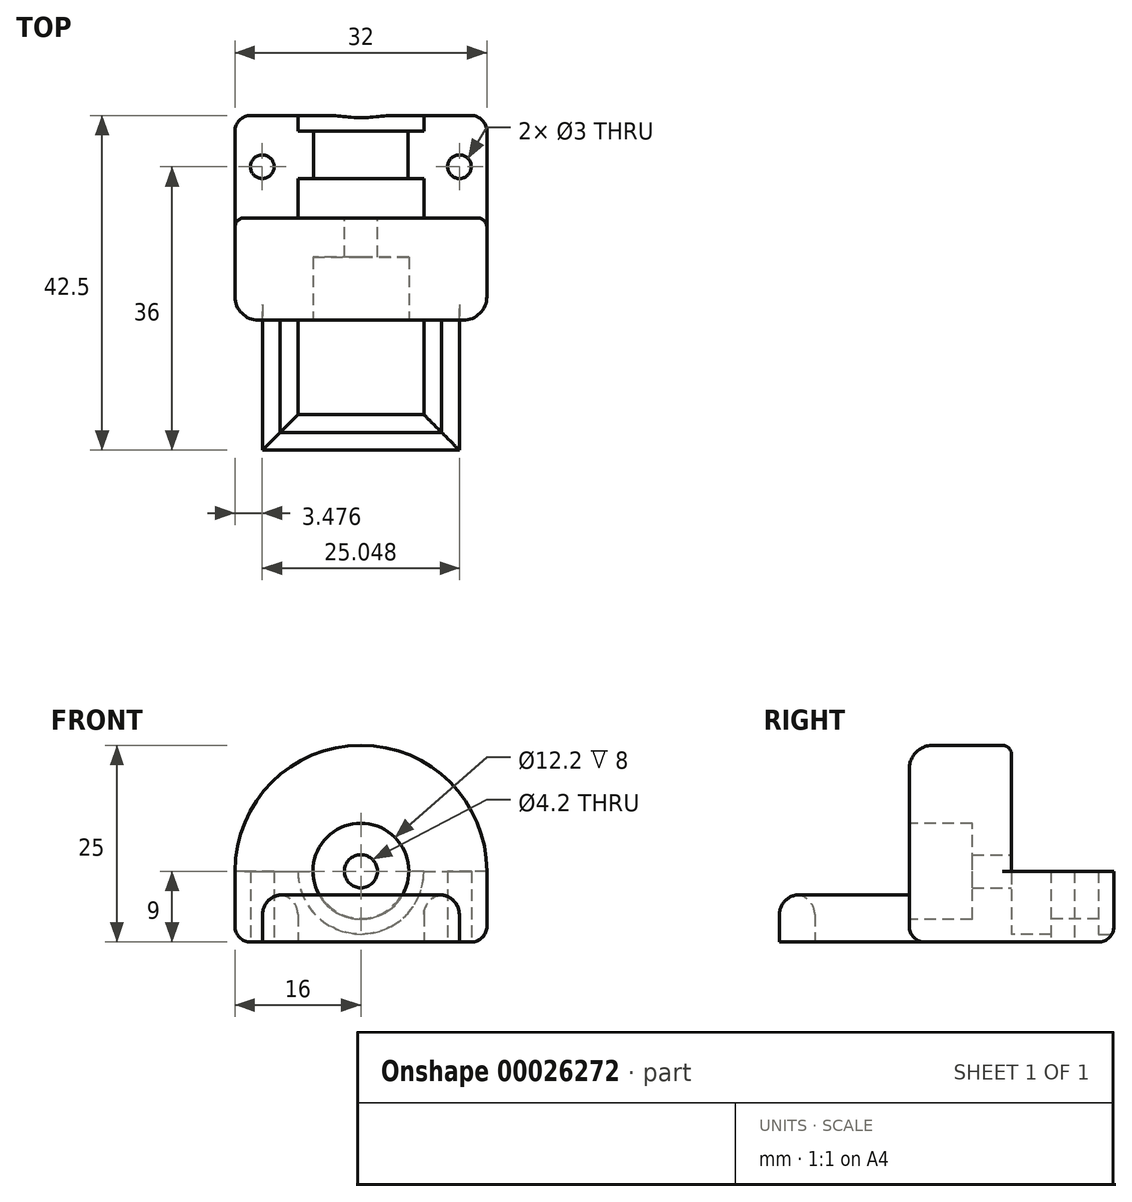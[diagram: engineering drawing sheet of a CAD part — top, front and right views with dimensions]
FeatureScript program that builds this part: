
annotation { "Feature Type Name" : "Feature", "Feature Type Description" : "" }
export const myFeature = defineFeature(function(context is Context, id is Id, definition is map)
    precondition{}
    {
        {
            var Q0;
            Q0=qCreatedBy(makeId("Top.planeOp"),FACE);
            var sketch = newSketch(context, id + "F0", { "sketchPlane" : qUnion([Q0])});
            skLineSegment(sketch, "E0.rect.bottom", {"start": v(-16, 6.5) * mm, "end": v(16, 6.5) * mm});
            skLineSegment(sketch, "E0.rect.top", {"start": v(-16, -6.5) * mm, "end": v(16, -6.5) * mm});
            skLineSegment(sketch, "E0.rect.left", {"start": v(-16, 6.5) * mm, "end": v(-16, -6.5) * mm});
            skLineSegment(sketch, "E0.rect.right", {"start": v(16, 6.5) * mm, "end": v(16, -6.5) * mm});
            skPoint(sketch, "E0.rect.middle", {"position": v(0, 0) * mm});
            skCircle(sketch, "E1", {"center": v(12.52, 0) * mm, "radius": 1.5 * mm});
            skCircle(sketch, "E2", {"center": v(-12.52, 0) * mm, "radius": 1.5 * mm});
            skSolve(sketch);
        }
        {
            var Q0;
            Q0=makeQuery(id+"F0.imprint","IMPRINT",FACE,{"disambiguationData":[TD([[makeQuery(id+"F0.imprint","IMPRINT",EDGE,{"derivedFrom":sQuery(id+"F0.wireOp",EDGE,"E0.rect.bottom")}),-1.0]])]});
            extrude(context, id + "F1", {"entities" : qUnion([Q0]), "depth" : 9 * mm});
        }
        {
            var Q0;
            Q0=makeQuery(id+"F1.opExtrude","SWEPT_FACE",FACE,{"disambiguationData":[OSD([sQuery(id+"F0.wireOp",EDGE,"E0.rect.top")])]});
            var sketch = newSketch(context, id + "F2", { "sketchPlane" : qUnion([Q0])});
            skCircle(sketch, "E3", {"center": v(0, 9) * mm, "radius": 8 * mm});
            skSolve(sketch);
        }
        {
            var Q0;
            Q0=qSketchRegion(id+"F2",true);
            var Q1;
            Q1=makeQuery(id+"F1.opExtrude","SWEPT_FACE",FACE,{"disambiguationData":[OSD([sQuery(id+"F0.wireOp",EDGE,"E0.rect.bottom")])]});
            extrude(context, id + "F3", {"entities" : qUnion([Q0, Q1]), "operationType" : NewBodyOperationType.REMOVE, "oppositeDirection" : true, "depth" : 5 * mm});
        }
        {
            var Q0;
            Q0=makeQuery(id+"F1.opExtrude","SWEPT_FACE",FACE,{"disambiguationData":[OSD([sQuery(id+"F0.wireOp",EDGE,"E0.rect.bottom")])]});
            var sketch = newSketch(context, id + "F4", { "sketchPlane" : qUnion([Q0])});
            skCircle(sketch, "E4", {"center": v(0, 9) * mm, "radius": 8 * mm});
            skSolve(sketch);
        }
        {
            var Q0;
            Q0=qSketchRegion(id+"F4",true);
            extrude(context, id + "F5", {"entities" : qUnion([Q0]), "operationType" : NewBodyOperationType.REMOVE, "oppositeDirection" : true, "depth" : 2 * mm});
        }
        {
            var Q0;
            Q0=makeQuery(id+"F5.boolean.opBoolean","COPY",FACE,{"derivedFrom":makeQuery(id+"F5.opExtrude","CAP_FACE",FACE,{"disambiguationData":[OSD([sQuery(id+"F4.wireOp",EDGE,"E4")])],"isStart":false})});
            var sketch = newSketch(context, id + "F6", { "sketchPlane" : qUnion([Q0])});
            skCircle(sketch, "E5", {"center": v(0, 9) * mm, "radius": 6 * mm});
            skSolve(sketch);
        }
        {
            var Q0;
            Q0=qSketchRegion(id+"F6",true);
            extrude(context, id + "F7", {"entities" : qUnion([Q0]), "operationType" : NewBodyOperationType.REMOVE, "oppositeDirection" : true, "depth" : 25 * mm});
        }
        {
            var Q0;
            Q0=makeQuery(id+"F1.opExtrude","CAP_EDGE",EDGE,{"disambiguationData":[OSD([sQuery(id+"F0.wireOp",EDGE,"E0.rect.bottom")])],"isStart":true});
            var Q1;
            Q1=makeQuery(id+"F7.boolean.opBoolean","COPY",EDGE,{"derivedFrom":makeQuery(id+"F7.opExtrude","CAP_EDGE",EDGE,{"disambiguationData":[OSD([sQuery(id+"F6.wireOp",EDGE,"E5")])],"isStart":true})});
            var Q2;
            Q2=makeQuery(id+"F1.opExtrude","SWEPT_EDGE",EDGE,{"disambiguationData":[OSD([sQuery(id+"F0.wireOp",EDGE,"E0.rect.bottom"),sQuery(id+"F0.wireOp",EDGE,"E0.rect.left")])]});
            var Q3;
            Q3=makeQuery(id+"F1.opExtrude","CAP_EDGE",EDGE,{"disambiguationData":[OSD([sQuery(id+"F0.wireOp",EDGE,"E0.rect.left")])],"isStart":true});
            var Q4;
            Q4=makeQuery(id+"F1.opExtrude","CAP_EDGE",EDGE,{"disambiguationData":[OSD([sQuery(id+"F0.wireOp",EDGE,"E0.rect.right")])],"isStart":true});
            var Q5;
            Q5=makeQuery(id+"F1.opExtrude","SWEPT_EDGE",EDGE,{"disambiguationData":[OSD([sQuery(id+"F0.wireOp",EDGE,"E0.rect.bottom"),sQuery(id+"F0.wireOp",EDGE,"E0.rect.right")])]});
            fillet(context, id + "F8", {"entities" : qUnion([Q0, Q1, Q2, Q3, Q4, Q5]), "radius" : 2 * mm, "tangentPropagation" : true, "allowEdgeOverflow" : false});
        }
        {
            var Q0;
            Q0=makeQuery(id+"F1.opExtrude","SWEPT_FACE",FACE,{"disambiguationData":[OSD([sQuery(id+"F0.wireOp",EDGE,"E0.rect.top")])]});
            var sketch = newSketch(context, id + "F9", { "sketchPlane" : qUnion([Q0])});
            skArc(sketch, "E6", {"start": v(16, 9) * mm, "mid": v(0, 25) * mm, "end": v(-16, 9) * mm});
            skLineSegment(sketch, "E7", {"start": v(0, 0) * mm, "end": v(13.23, 0) * mm});
            skLineSegment(sketch, "E8", {"start": v(-13.23, 0) * mm, "end": v(0, 0) * mm});
            skLineSegment(sketch, "E9", {"start": v(-16, 9) * mm, "end": v(-16, 0) * mm});
            skLineSegment(sketch, "E10", {"start": v(16, 9) * mm, "end": v(16, 0) * mm});
            skLineSegment(sketch, "E11", {"start": v(-16, 0) * mm, "end": v(16, 0) * mm});
            skSolve(sketch);
        }
        {
            var Q0;
            Q0=qSketchRegion(id+"F9",true);
            extrude(context, id + "F10", {"entities" : qUnion([Q0]), "operationType" : NewBodyOperationType.ADD, "depth" : 13 * mm});
        }
        {
            var Q0;
            Q0=qCreatedBy(makeId("Top.planeOp"),FACE);
            var sketch = newSketch(context, id + "F11", { "sketchPlane" : qUnion([Q0])});
            skLineSegment(sketch, "E12", {"start": v(-8, -19.5) * mm, "end": v(-12.5, -19.5) * mm});
            skLineSegment(sketch, "E13", {"start": v(-12.5, -19.5) * mm, "end": v(-8, -19.5) * mm});
            skLineSegment(sketch, "E14", {"start": v(12.5, -19.5) * mm, "end": v(12.5, -36) * mm});
            skLineSegment(sketch, "E15", {"start": v(12.5, -36) * mm, "end": v(-12.5, -36) * mm});
            skLineSegment(sketch, "E16", {"start": v(-12.5, -36) * mm, "end": v(-12.5, -19.5) * mm});
            skLineSegment(sketch, "E17", {"start": v(-8, -19.5) * mm, "end": v(-8, -31.5) * mm});
            skLineSegment(sketch, "E18", {"start": v(-8, -31.5) * mm, "end": v(8, -31.5) * mm});
            skLineSegment(sketch, "E19", {"start": v(8, -31.5) * mm, "end": v(8, -19.5) * mm});
            skLineSegment(sketch, "E20.trimOffspring", {"start": v(8, -19.5) * mm, "end": v(12.5, -19.5) * mm});
            skPoint(sketch, "E21.orphan", {"position": v(0, -19.5) * mm});
            skPoint(sketch, "E22", {"position": v(0, -31.5) * mm});
            skPoint(sketch, "E23", {"position": v(0, -36) * mm});
            skSolve(sketch);
        }
        {
            var Q0;
            Q0=qSketchRegion(id+"F11",true);
            extrude(context, id + "F12", {"entities" : qUnion([Q0]), "operationType" : NewBodyOperationType.ADD, "depth" : 6 * mm});
        }
        {
            var Q0;
            Q0=makeQuery(id+"F12.opExtrude","CAP_EDGE",EDGE,{"disambiguationData":[OSD([sQuery(id+"F11.wireOp",EDGE,"E17")])],"isStart":false});
            var Q1;
            Q1=makeQuery(id+"F12.opExtrude","CAP_EDGE",EDGE,{"disambiguationData":[OSD([sQuery(id+"F11.wireOp",EDGE,"E16")])],"isStart":false});
            var Q2;
            Q2=makeQuery(id+"F12.opExtrude","CAP_EDGE",EDGE,{"disambiguationData":[OSD([sQuery(id+"F11.wireOp",EDGE,"E19")])],"isStart":false});
            var Q3;
            Q3=makeQuery(id+"F12.opExtrude","CAP_EDGE",EDGE,{"disambiguationData":[OSD([sQuery(id+"F11.wireOp",EDGE,"E14")])],"isStart":false});
            var Q4;
            Q4=makeQuery(id+"F12.opExtrude","CAP_EDGE",EDGE,{"disambiguationData":[OSD([sQuery(id+"F11.wireOp",EDGE,"E18")])],"isStart":false});
            var Q5;
            Q5=makeQuery(id+"F12.opExtrude","CAP_EDGE",EDGE,{"disambiguationData":[OSD([sQuery(id+"F11.wireOp",EDGE,"E15")])],"isStart":false});
            fillet(context, id + "F13", {"entities" : qUnion([Q0, Q1, Q2, Q3, Q4, Q5]), "radius" : 2.5 * mm, "tangentPropagation" : true, "allowEdgeOverflow" : false});
        }
        {
            var Q0;
            Q0=makeQuery(id+"F10.opExtrude","CAP_EDGE",EDGE,{"disambiguationData":[OSD([sQuery(id+"F9.wireOp",EDGE,"E6")])],"isStart":false});
            fillet(context, id + "F14", {"entities" : qUnion([Q0]), "radius" : 3 * mm, "tangentPropagation" : true, "allowEdgeOverflow" : false});
        }
        {
            var Q0;
            Q0=makeQuery(id+"F10.opExtrude","CAP_EDGE",EDGE,{"disambiguationData":[OSD([sQuery(id+"F9.wireOp",EDGE,"E6")])],"isStart":true});
            fillet(context, id + "F15", {"entities" : qUnion([Q0]), "radius" : 1.2 * mm, "tangentPropagation" : true, "allowEdgeOverflow" : false});
        }
        {
            var Q0;
            Q0=makeQuery(id+"F10.opExtrude","CAP_FACE",FACE,{"disambiguationData":[OSD([sQuery(id+"F9.wireOp",EDGE,"E6"),sQuery(id+"F9.wireOp",EDGE,"E9"),sQuery(id+"F9.wireOp",EDGE,"E10"),sQuery(id+"F9.wireOp",EDGE,"E11")])],"isStart":false});
            var sketch = newSketch(context, id + "F16", { "sketchPlane" : qUnion([Q0])});
            skCircle(sketch, "E24", {"center": v(0, 9) * mm, "radius": 6.1 * mm});
            skSolve(sketch);
        }
        {
            var Q0;
            Q0=qSketchRegion(id+"F16",true);
            extrude(context, id + "F17", {"entities" : qUnion([Q0]), "operationType" : NewBodyOperationType.REMOVE, "oppositeDirection" : true, "depth" : 8 * mm});
        }
        {
            var Q0;
            Q0=makeQuery(id+"F14.opFillet","BLEND_EDGE",EDGE,{"blendedFrom":[makeQuery(id+"F10.opExtrude","CAP_EDGE",EDGE,{"disambiguationData":[OSD([sQuery(id+"F9.wireOp",EDGE,"E9")])],"isStart":false}),makeQuery(id+"F10.boolean.opBoolean","MERGE",FACE,{"derivedFrom":[makeQuery(id+"F1.opExtrude","CAP_FACE",FACE,{"disambiguationData":[OSD([sQuery(id+"F0.wireOp",EDGE,"E0.rect.bottom"),sQuery(id+"F0.wireOp",EDGE,"E0.rect.top"),sQuery(id+"F0.wireOp",EDGE,"E0.rect.left"),sQuery(id+"F0.wireOp",EDGE,"E0.rect.right"),sQuery(id+"F0.wireOp",EDGE,"E1"),sQuery(id+"F0.wireOp",EDGE,"E2")])],"isStart":true}),makeQuery(id+"F10.opExtrude","SWEPT_FACE",FACE,{"disambiguationData":[OSD([sQuery(id+"F9.wireOp",EDGE,"E11")])]})]})],"blendedInto":[makeQuery(id+"F10.boolean.opBoolean","MERGE",FACE,{"derivedFrom":[makeQuery(id+"F1.opExtrude","CAP_FACE",FACE,{"disambiguationData":[OSD([sQuery(id+"F0.wireOp",EDGE,"E0.rect.bottom"),sQuery(id+"F0.wireOp",EDGE,"E0.rect.top"),sQuery(id+"F0.wireOp",EDGE,"E0.rect.left"),sQuery(id+"F0.wireOp",EDGE,"E0.rect.right"),sQuery(id+"F0.wireOp",EDGE,"E1"),sQuery(id+"F0.wireOp",EDGE,"E2")])],"isStart":true}),makeQuery(id+"F10.opExtrude","SWEPT_FACE",FACE,{"disambiguationData":[OSD([sQuery(id+"F9.wireOp",EDGE,"E11")])]})]})]});
            fillet(context, id + "F18", {"entities" : qUnion([Q0]), "radius" : 2 * mm, "tangentPropagation" : true, "allowEdgeOverflow" : false});
        }
        {
            var Q0;
            {var subQ0=sQuery(id+"F9.wireOp",EDGE,"E6");var subQ1=sQuery(id+"F9.wireOp",EDGE,"E9");var subQ2=sQuery(id+"F9.wireOp",EDGE,"E10");Q0=makeQuery(id+"F10.boolean.opBoolean","SPLIT",FACE,{"disambiguationData":[TD([makeQuery(id+"F3.boolean.opBoolean","COPY",FACE,{"derivedFrom":makeQuery(id+"F3.opExtrude","SWEPT_FACE",FACE,{"disambiguationData":[OSD([sQuery(id+"F2.wireOp",EDGE,"E3")])]})})])],"derivedFrom":makeQuery(id+"F10.opExtrude","CAP_FACE",FACE,{"disambiguationData":[OSD([subQ0,subQ1,subQ2,sQuery(id+"F9.wireOp",EDGE,"E11")])],"isStart":true})});}
            var sketch = newSketch(context, id + "F19", { "sketchPlane" : qUnion([Q0])});
            skCircle(sketch, "E25", {"center": v(0, 9) * mm, "radius": 2.1 * mm});
            skSolve(sketch);
        }
        {
            var Q0;
            Q0=qSketchRegion(id+"F19",true);
            extrude(context, id + "F20", {"entities" : qUnion([Q0]), "operationType" : NewBodyOperationType.REMOVE, "oppositeDirection" : true, "depth" : 7 * mm});
        }
        {
            var Q0;
            Q0=makeQuery(id+"F10.opExtrude","SWEPT_EDGE",EDGE,{"disambiguationData":[OSD([sQuery(id+"F9.wireOp",EDGE,"E10"),sQuery(id+"F9.wireOp",EDGE,"E11")])]});
            fillet(context, id + "F21", {"entities" : qUnion([Q0]), "radius" : 2 * mm, "tangentPropagation" : true, "allowEdgeOverflow" : false});
        }
    });
